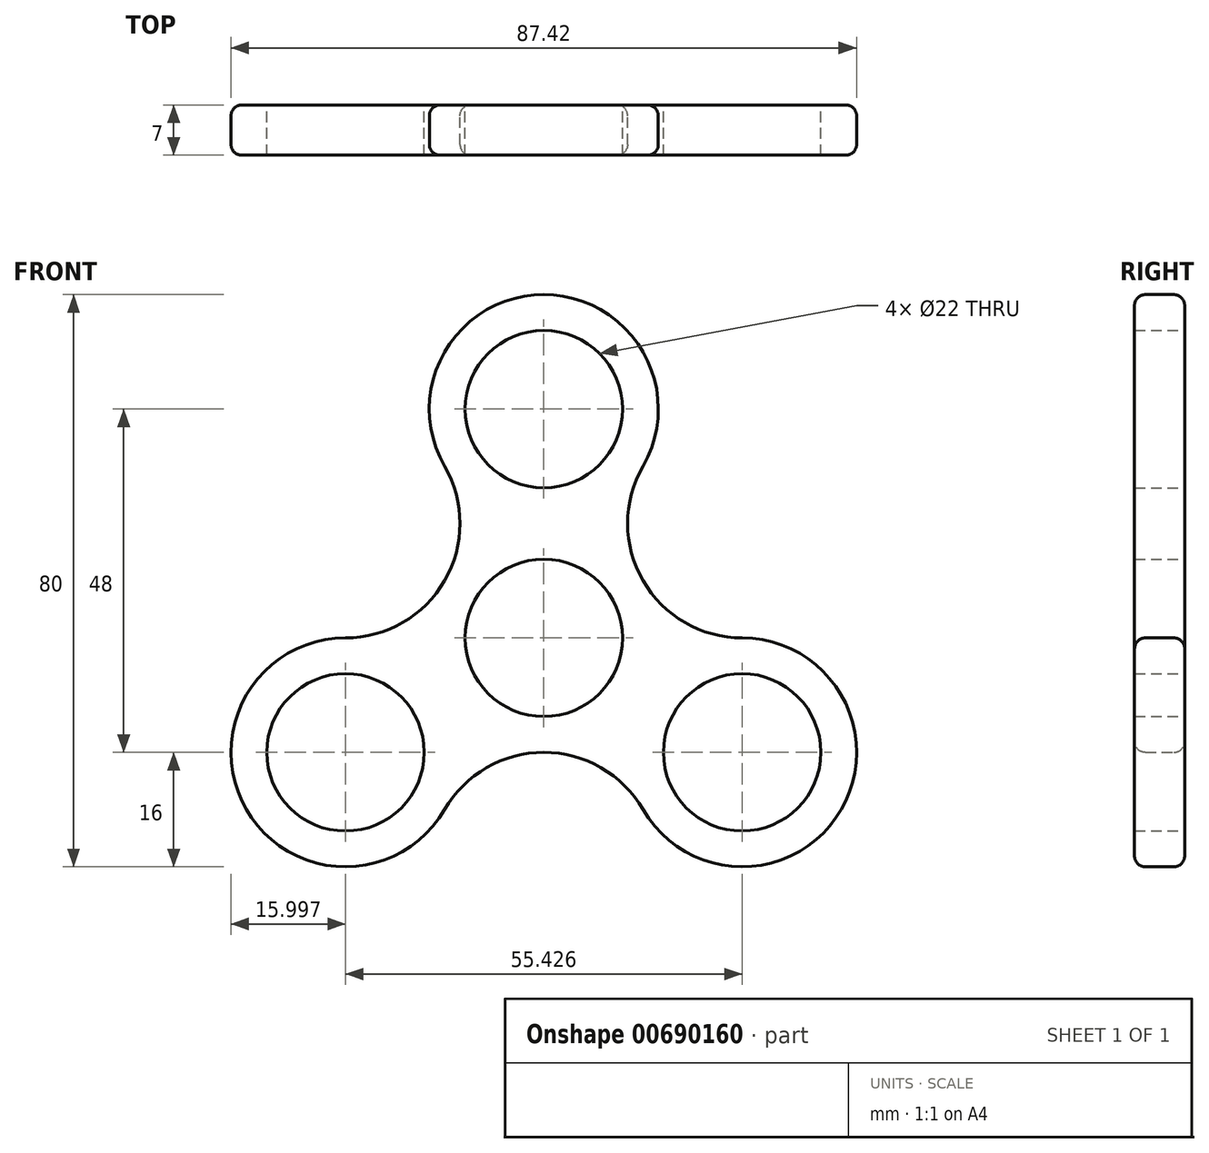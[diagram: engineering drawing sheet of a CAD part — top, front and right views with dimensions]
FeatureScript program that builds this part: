
annotation { "Feature Type Name" : "Feature", "Feature Type Description" : "" }
export const myFeature = defineFeature(function(context is Context, id is Id, definition is map)
    precondition{}
    {
        {
            var Q0;
            Q0=qCreatedBy(makeId("Front.planeOp"),FACE);
            var sketch = newSketch(context, id + "F0", { "sketchPlane" : qUnion([Q0])});
            skCircle(sketch, "E0", {"center": v(0, 0) * mm, "radius": 11 * mm});
            skArc(sketch, "E1", {"start": v(13.86, 24) * mm, "mid": v(0, 48) * mm, "end": v(-13.86, 24) * mm});
            skArc(sketch, "E2.MirrorC", {"start": v(-13.86, -24) * mm, "mid": v(0, -16) * mm, "end": v(13.86, -24) * mm});
            skArc(sketch, "E3.MirrorC", {"start": v(27.71, 0) * mm, "mid": v(41.57, -24) * mm, "end": v(13.86, -24) * mm});
            skArc(sketch, "E4", {"start": v(13.86, 24) * mm, "mid": v(13.86, 8) * mm, "end": v(27.71, 0) * mm});
            skArc(sketch, "E5.MirrorC", {"start": v(-27.71, 0) * mm, "mid": v(-41.57, -24) * mm, "end": v(-13.86, -24) * mm});
            skArc(sketch, "E6.MirrorC", {"start": v(-13.86, 24) * mm, "mid": v(-13.86, 8) * mm, "end": v(-27.71, 0) * mm});
            skCircle(sketch, "E7", {"center": v(0, 32) * mm, "radius": 11 * mm});
            skCircle(sketch, "E8", {"center": v(-27.71, -16) * mm, "radius": 11 * mm});
            skCircle(sketch, "E9", {"center": v(27.71, -16) * mm, "radius": 11 * mm});
            skSolve(sketch);
        }
        {
            var Q0;
            Q0 = qSketchRegion(id + "F0", true);
            extrude(context, id + "F1", {"entities" : qUnion([Q0]), "depth" : 7 * mm, "offsetDistance" : 25 * mm});
        }
        {
            var Q0;
            Q0=makeQuery(id+"F1.opExtrude","SWEPT_FACE",FACE,{"disambiguationData":[OSD([sQuery(id+"F0.wireOp",EDGE,"E4")])]});
            var Q1;
            Q1=makeQuery(id+"F1.opExtrude","SWEPT_FACE",FACE,{"disambiguationData":[OSD([sQuery(id+"F0.wireOp",EDGE,"E3.MirrorC")])]});
            var Q2;
            Q2=makeQuery(id+"F1.opExtrude","SWEPT_FACE",FACE,{"disambiguationData":[OSD([sQuery(id+"F0.wireOp",EDGE,"E1")])]});
            var Q3;
            Q3=makeQuery(id+"F1.opExtrude","CAP_EDGE",EDGE,{"disambiguationData":[OSD([sQuery(id+"F0.wireOp",EDGE,"E6.MirrorC")])],"isStart":false});
            var Q4;
            Q4=makeQuery(id+"F1.opExtrude","SWEPT_FACE",FACE,{"disambiguationData":[OSD([sQuery(id+"F0.wireOp",EDGE,"E6.MirrorC")])]});
            var Q5;
            Q5=makeQuery(id+"F1.opExtrude","SWEPT_FACE",FACE,{"disambiguationData":[OSD([sQuery(id+"F0.wireOp",EDGE,"E5.MirrorC")])]});
            var Q6;
            Q6=makeQuery(id+"F1.opExtrude","SWEPT_FACE",FACE,{"disambiguationData":[OSD([sQuery(id+"F0.wireOp",EDGE,"E2.MirrorC")])]});
            fillet(context, id + "F2", {"entities" : qUnion([Q0, Q1, Q2, Q3, Q4, Q5, Q6]), "radius" : 1.5 * mm, "tangentPropagation" : true, "allowEdgeOverflow" : false});
        }
    });
